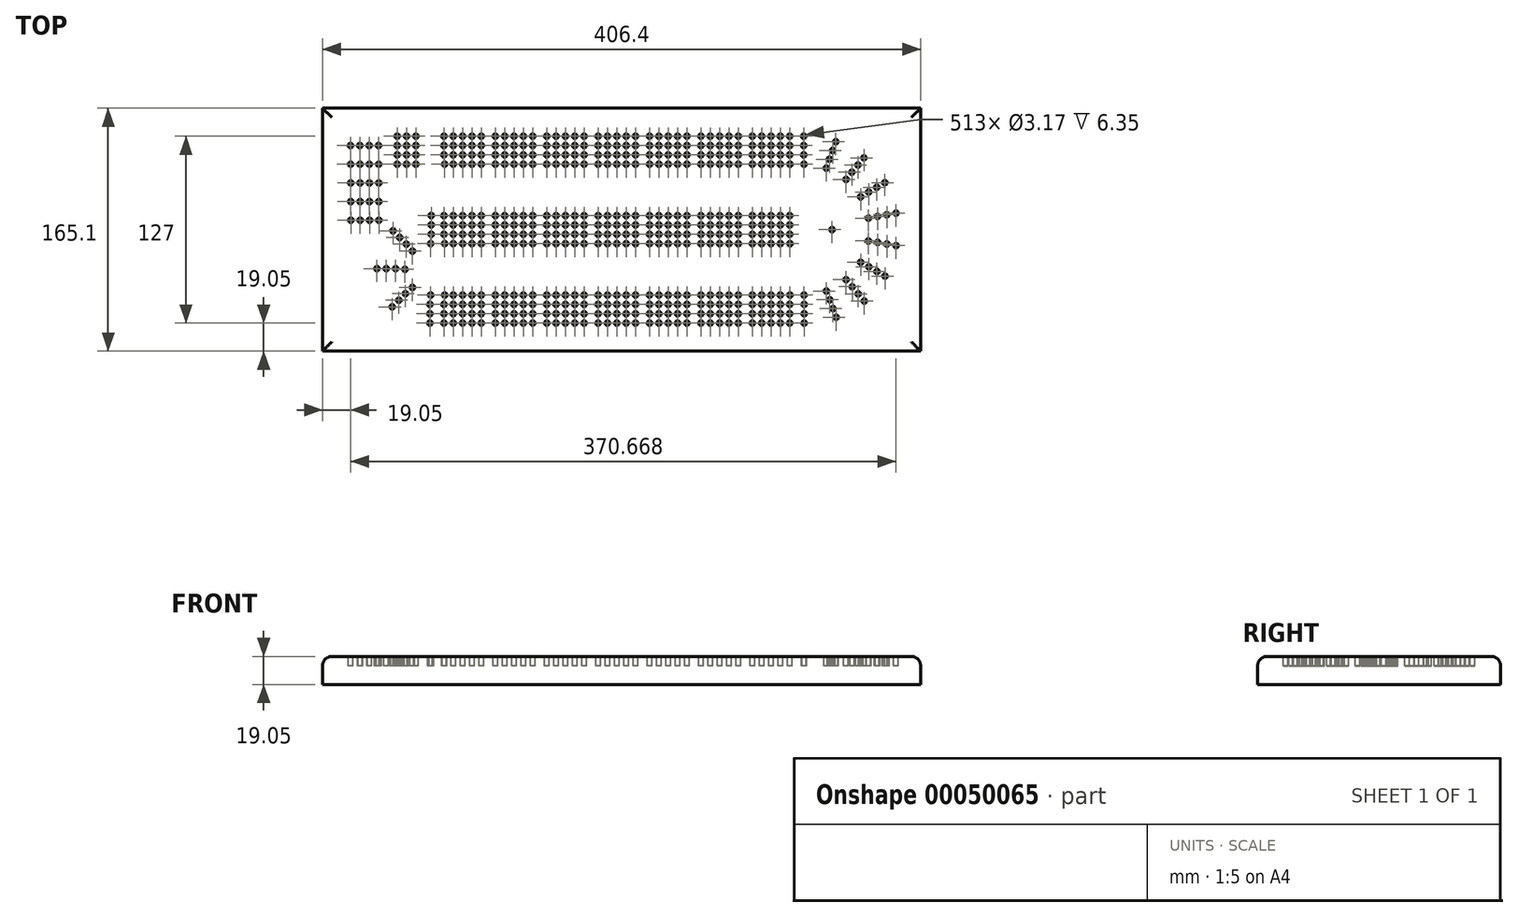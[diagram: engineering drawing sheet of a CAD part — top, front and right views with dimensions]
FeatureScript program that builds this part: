
annotation { "Feature Type Name" : "Feature", "Feature Type Description" : "" }
export const myFeature = defineFeature(function(context is Context, id is Id, definition is map)
    precondition{}
    {
        {
            var Q0;
            Q0=qCreatedBy(makeId("Top.planeOp"),FACE);
            var sketch = newSketch(context, id + "F0", { "sketchPlane" : qUnion([Q0])});
            skLineSegment(sketch, "E0.bottom", {"start": v(0, 0) * mm, "end": v(406.4, 0) * mm});
            skLineSegment(sketch, "E0.top", {"start": v(0, 165.1) * mm, "end": v(406.4, 165.1) * mm});
            skLineSegment(sketch, "E0.left", {"start": v(0, 0) * mm, "end": v(0, 165.1) * mm});
            skLineSegment(sketch, "E0.right", {"start": v(406.4, 0) * mm, "end": v(406.4, 165.1) * mm});
            skSolve(sketch);
        }
        {
            var Q0;
            Q0 = qSketchRegion(id + "F0", true);
            extrude(context, id + "F1", {"entities" : qUnion([Q0]), "depth" : 19.05 * mm});
        }
        {
            var Q0;
            Q0=makeQuery(id+"F1.opExtrude","CAP_EDGE",EDGE,{"disambiguationData":[OSD([sQuery(id+"F0.wireOp",EDGE,"E0.left")])],"isStart":false});
            var Q1;
            Q1=makeQuery(id+"F1.opExtrude","CAP_EDGE",EDGE,{"disambiguationData":[OSD([sQuery(id+"F0.wireOp",EDGE,"E0.top")])],"isStart":false});
            var Q2;
            Q2=makeQuery(id+"F1.opExtrude","CAP_EDGE",EDGE,{"disambiguationData":[OSD([sQuery(id+"F0.wireOp",EDGE,"E0.bottom")])],"isStart":false});
            var Q3;
            Q3=makeQuery(id+"F1.opExtrude","CAP_EDGE",EDGE,{"disambiguationData":[OSD([sQuery(id+"F0.wireOp",EDGE,"E0.right")])],"isStart":false});
            fillet(context, id + "F2", {"entities" : qUnion([Q0, Q1, Q2, Q3]), "radius" : 6.35 * mm, "tangentPropagation" : true, "allowEdgeOverflow" : false});
        }
        {
            var Q0;
            Q0=makeQuery(id+"F1.opExtrude","CAP_FACE",FACE,{"disambiguationData":[OSD([sQuery(id+"F0.wireOp",EDGE,"E0.bottom"),sQuery(id+"F0.wireOp",EDGE,"E0.top"),sQuery(id+"F0.wireOp",EDGE,"E0.left"),sQuery(id+"F0.wireOp",EDGE,"E0.right")])],"isStart":false});
            var sketch = newSketch(context, id + "F3", { "sketchPlane" : qUnion([Q0])});
            skLineSegment(sketch, "E1", {"start": v(6.35, 158.75) * mm, "end": v(6.35, 139.7) * mm});
            skLineSegment(sketch, "E2", {"start": v(6.35, 139.7) * mm, "end": v(19.05, 139.7) * mm});
            skLineSegment(sketch, "E3", {"start": v(19.05, 139.7) * mm, "end": v(25.4, 139.7) * mm});
            skLineSegment(sketch, "E4", {"start": v(25.4, 139.7) * mm, "end": v(31.75, 139.7) * mm});
            skLineSegment(sketch, "E5", {"start": v(31.75, 139.7) * mm, "end": v(38.1, 139.7) * mm});
            skLineSegment(sketch, "E6", {"start": v(6.35, 158.75) * mm, "end": v(50.8, 158.75) * mm});
            skCircle(sketch, "E7", {"center": v(19.05, 139.7) * mm, "radius": 1.59 * mm});
            skCircle(sketch, "E8", {"center": v(25.4, 139.7) * mm, "radius": 1.59 * mm});
            skCircle(sketch, "E9", {"center": v(31.75, 139.7) * mm, "radius": 1.59 * mm});
            skCircle(sketch, "E10", {"center": v(38.1, 139.7) * mm, "radius": 1.59 * mm});
            skCircle(sketch, "E11", {"center": v(50.8, 146.05) * mm, "radius": 1.59 * mm});
            skCircle(sketch, "E12", {"center": v(50.8, 139.7) * mm, "radius": 1.59 * mm});
            skCircle(sketch, "E13", {"center": v(50.8, 133.35) * mm, "radius": 1.59 * mm});
            skCircle(sketch, "E14", {"center": v(50.8, 127) * mm, "radius": 1.59 * mm});
            skCircle(sketch, "E15.1.0.0", {"center": v(31.8, 127) * mm, "radius": 1.59 * mm});
            skCircle(sketch, "E15.1.0.1", {"center": v(25.45, 127) * mm, "radius": 1.59 * mm});
            skCircle(sketch, "E15.1.0.2", {"center": v(19.1, 127) * mm, "radius": 1.59 * mm});
            skCircle(sketch, "E15.1.0.3", {"center": v(38.15, 127) * mm, "radius": 1.59 * mm});
            skCircle(sketch, "E15.2.0.0", {"center": v(31.84, 114.3) * mm, "radius": 1.59 * mm});
            skCircle(sketch, "E15.2.0.1", {"center": v(25.5, 114.3) * mm, "radius": 1.59 * mm});
            skCircle(sketch, "E15.2.0.2", {"center": v(19.14, 114.3) * mm, "radius": 1.59 * mm});
            skCircle(sketch, "E15.2.0.3", {"center": v(38.2, 114.3) * mm, "radius": 1.59 * mm});
            skCircle(sketch, "E15.3.0.0", {"center": v(31.89, 101.6) * mm, "radius": 1.59 * mm});
            skCircle(sketch, "E15.3.0.1", {"center": v(25.54, 101.6) * mm, "radius": 1.59 * mm});
            skCircle(sketch, "E15.3.0.2", {"center": v(19.19, 101.6) * mm, "radius": 1.59 * mm});
            skCircle(sketch, "E15.3.0.3", {"center": v(38.24, 101.6) * mm, "radius": 1.59 * mm});
            skCircle(sketch, "E15.4.0.0", {"center": v(31.93, 88.9) * mm, "radius": 1.59 * mm});
            skCircle(sketch, "E15.4.0.1", {"center": v(25.58, 88.9) * mm, "radius": 1.59 * mm});
            skCircle(sketch, "E15.4.0.2", {"center": v(19.23, 88.9) * mm, "radius": 1.59 * mm});
            skCircle(sketch, "E15.4.0.3", {"center": v(38.28, 88.9) * mm, "radius": 1.59 * mm});
            skLineSegment(sketch, "E15.direction1", {"start": v(31.75, 139.7) * mm, "end": v(31.8, 127) * mm, "construction": true});
            skCircle(sketch, "E16.1.0.0", {"center": v(57.15, 146.05) * mm, "radius": 1.59 * mm});
            skCircle(sketch, "E16.1.0.1", {"center": v(57.15, 139.7) * mm, "radius": 1.59 * mm});
            skCircle(sketch, "E16.1.0.2", {"center": v(57.15, 133.35) * mm, "radius": 1.59 * mm});
            skCircle(sketch, "E16.1.0.3", {"center": v(57.15, 127) * mm, "radius": 1.59 * mm});
            skCircle(sketch, "E16.2.0.0", {"center": v(63.5, 146.05) * mm, "radius": 1.59 * mm});
            skCircle(sketch, "E16.2.0.1", {"center": v(63.5, 139.7) * mm, "radius": 1.59 * mm});
            skCircle(sketch, "E16.2.0.2", {"center": v(63.5, 133.35) * mm, "radius": 1.59 * mm});
            skCircle(sketch, "E16.2.0.3", {"center": v(63.5, 127) * mm, "radius": 1.59 * mm});
            skLineSegment(sketch, "E16.direction1", {"start": v(50.8, 146.05) * mm, "end": v(57.15, 146.05) * mm, "construction": true});
            skCircle(sketch, "E17.1.0.0", {"center": v(95.25, 133.35) * mm, "radius": 1.59 * mm});
            skCircle(sketch, "E17.1.0.1", {"center": v(88.9, 139.7) * mm, "radius": 1.59 * mm});
            skLineSegment(sketch, "E17.1.0.2", {"start": v(82.55, 146.05) * mm, "end": v(88.9, 146.05) * mm, "construction": true});
            skCircle(sketch, "E17.1.0.3", {"center": v(88.9, 146.05) * mm, "radius": 1.59 * mm});
            skCircle(sketch, "E17.1.0.4", {"center": v(82.55, 133.35) * mm, "radius": 1.59 * mm});
            skCircle(sketch, "E17.1.0.5", {"center": v(82.55, 139.7) * mm, "radius": 1.59 * mm});
            skCircle(sketch, "E17.1.0.6", {"center": v(82.55, 146.05) * mm, "radius": 1.59 * mm});
            skCircle(sketch, "E17.1.0.7", {"center": v(95.25, 139.7) * mm, "radius": 1.59 * mm});
            skCircle(sketch, "E17.1.0.8", {"center": v(95.25, 146.05) * mm, "radius": 1.59 * mm});
            skCircle(sketch, "E17.1.0.9", {"center": v(88.9, 133.35) * mm, "radius": 1.59 * mm});
            skCircle(sketch, "E17.1.0.10", {"center": v(82.97, 127) * mm, "radius": 1.59 * mm});
            skCircle(sketch, "E17.1.0.11", {"center": v(95.25, 127) * mm, "radius": 1.59 * mm});
            skCircle(sketch, "E17.1.0.12", {"center": v(88.9, 127) * mm, "radius": 1.59 * mm});
            skCircle(sketch, "E18.1.0.0", {"center": v(101.6, 139.7) * mm, "radius": 1.59 * mm});
            skCircle(sketch, "E18.1.0.2", {"center": v(101.6, 133.35) * mm, "radius": 1.59 * mm});
            skCircle(sketch, "E18.1.0.3", {"center": v(101.6, 127) * mm, "radius": 1.59 * mm});
            skCircle(sketch, "E18.1.0.4", {"center": v(101.6, 146.05) * mm, "radius": 1.59 * mm});
            skCircle(sketch, "E18.2.0.0", {"center": v(107.95, 139.7) * mm, "radius": 1.59 * mm});
            skCircle(sketch, "E18.2.0.2", {"center": v(107.95, 133.35) * mm, "radius": 1.59 * mm});
            skCircle(sketch, "E18.2.0.3", {"center": v(107.95, 127) * mm, "radius": 1.59 * mm});
            skCircle(sketch, "E18.2.0.4", {"center": v(107.95, 146.05) * mm, "radius": 1.59 * mm});
            skCircle(sketch, "E19.1.0.0", {"center": v(142.88, 146.05) * mm, "radius": 1.59 * mm});
            skCircle(sketch, "E19.1.0.1", {"center": v(117.47, 146.05) * mm, "radius": 1.59 * mm});
            skCircle(sketch, "E19.1.0.2", {"center": v(136.52, 139.7) * mm, "radius": 1.59 * mm});
            skCircle(sketch, "E19.1.0.3", {"center": v(123.82, 146.05) * mm, "radius": 1.59 * mm});
            skCircle(sketch, "E19.1.0.4", {"center": v(117.47, 127) * mm, "radius": 1.59 * mm});
            skCircle(sketch, "E19.1.0.6", {"center": v(142.87, 133.35) * mm, "radius": 1.59 * mm});
            skCircle(sketch, "E19.1.0.7", {"center": v(117.47, 133.35) * mm, "radius": 1.59 * mm});
            skCircle(sketch, "E19.1.0.8", {"center": v(130.17, 127) * mm, "radius": 1.59 * mm});
            skCircle(sketch, "E19.1.0.9", {"center": v(123.82, 127) * mm, "radius": 1.59 * mm});
            skCircle(sketch, "E19.1.0.10", {"center": v(142.87, 127) * mm, "radius": 1.59 * mm});
            skCircle(sketch, "E19.1.0.11", {"center": v(117.47, 139.7) * mm, "radius": 1.59 * mm});
            skCircle(sketch, "E19.1.0.13", {"center": v(130.17, 139.7) * mm, "radius": 1.59 * mm});
            skCircle(sketch, "E19.1.0.14", {"center": v(136.52, 133.35) * mm, "radius": 1.59 * mm});
            skCircle(sketch, "E19.1.0.15", {"center": v(136.53, 146.05) * mm, "radius": 1.59 * mm});
            skCircle(sketch, "E19.1.0.16", {"center": v(123.83, 139.7) * mm, "radius": 1.59 * mm});
            skCircle(sketch, "E19.1.0.17", {"center": v(130.18, 146.05) * mm, "radius": 1.59 * mm});
            skLineSegment(sketch, "E19.1.0.18", {"start": v(117.47, 146.05) * mm, "end": v(123.82, 146.05) * mm, "construction": true});
            skCircle(sketch, "E19.1.0.19", {"center": v(123.82, 133.35) * mm, "radius": 1.59 * mm});
            skCircle(sketch, "E19.1.0.20", {"center": v(142.87, 139.7) * mm, "radius": 1.59 * mm});
            skCircle(sketch, "E19.1.0.21", {"center": v(136.52, 127) * mm, "radius": 1.59 * mm});
            skCircle(sketch, "E19.1.0.22", {"center": v(130.17, 133.35) * mm, "radius": 1.59 * mm});
            skCircle(sketch, "E19.2.0.0", {"center": v(177.8, 146.05) * mm, "radius": 1.59 * mm});
            skCircle(sketch, "E19.2.0.1", {"center": v(152.4, 146.05) * mm, "radius": 1.59 * mm});
            skCircle(sketch, "E19.2.0.2", {"center": v(171.45, 139.7) * mm, "radius": 1.59 * mm});
            skCircle(sketch, "E19.2.0.3", {"center": v(158.75, 146.05) * mm, "radius": 1.59 * mm});
            skCircle(sketch, "E19.2.0.4", {"center": v(152.4, 127) * mm, "radius": 1.59 * mm});
            skCircle(sketch, "E19.2.0.6", {"center": v(177.8, 133.35) * mm, "radius": 1.59 * mm});
            skCircle(sketch, "E19.2.0.7", {"center": v(152.4, 133.35) * mm, "radius": 1.59 * mm});
            skCircle(sketch, "E19.2.0.8", {"center": v(165.1, 127) * mm, "radius": 1.59 * mm});
            skCircle(sketch, "E19.2.0.9", {"center": v(158.75, 127) * mm, "radius": 1.59 * mm});
            skCircle(sketch, "E19.2.0.10", {"center": v(177.8, 127) * mm, "radius": 1.59 * mm});
            skCircle(sketch, "E19.2.0.11", {"center": v(152.4, 139.7) * mm, "radius": 1.59 * mm});
            skCircle(sketch, "E19.2.0.13", {"center": v(165.1, 139.7) * mm, "radius": 1.59 * mm});
            skCircle(sketch, "E19.2.0.14", {"center": v(171.45, 133.35) * mm, "radius": 1.59 * mm});
            skCircle(sketch, "E19.2.0.15", {"center": v(171.45, 146.05) * mm, "radius": 1.59 * mm});
            skCircle(sketch, "E19.2.0.16", {"center": v(158.75, 139.7) * mm, "radius": 1.59 * mm});
            skCircle(sketch, "E19.2.0.17", {"center": v(165.1, 146.05) * mm, "radius": 1.59 * mm});
            skCircle(sketch, "E19.2.0.19", {"center": v(158.75, 133.35) * mm, "radius": 1.59 * mm});
            skCircle(sketch, "E19.2.0.20", {"center": v(177.8, 139.7) * mm, "radius": 1.59 * mm});
            skCircle(sketch, "E19.2.0.21", {"center": v(171.45, 127) * mm, "radius": 1.59 * mm});
            skCircle(sketch, "E19.2.0.22", {"center": v(165.1, 133.35) * mm, "radius": 1.59 * mm});
            skCircle(sketch, "E19.3.0.0", {"center": v(212.72, 146.05) * mm, "radius": 1.59 * mm});
            skCircle(sketch, "E19.3.0.1", {"center": v(187.32, 146.05) * mm, "radius": 1.59 * mm});
            skCircle(sketch, "E19.3.0.2", {"center": v(206.37, 139.7) * mm, "radius": 1.59 * mm});
            skCircle(sketch, "E19.3.0.3", {"center": v(193.67, 146.05) * mm, "radius": 1.59 * mm});
            skCircle(sketch, "E19.3.0.4", {"center": v(187.32, 127) * mm, "radius": 1.59 * mm});
            skCircle(sketch, "E19.3.0.6", {"center": v(212.72, 133.35) * mm, "radius": 1.59 * mm});
            skCircle(sketch, "E19.3.0.7", {"center": v(187.32, 133.35) * mm, "radius": 1.59 * mm});
            skCircle(sketch, "E19.3.0.8", {"center": v(200.02, 127) * mm, "radius": 1.59 * mm});
            skCircle(sketch, "E19.3.0.9", {"center": v(193.67, 127) * mm, "radius": 1.59 * mm});
            skCircle(sketch, "E19.3.0.10", {"center": v(212.72, 127) * mm, "radius": 1.59 * mm});
            skCircle(sketch, "E19.3.0.11", {"center": v(187.32, 139.7) * mm, "radius": 1.59 * mm});
            skCircle(sketch, "E19.3.0.13", {"center": v(200.02, 139.7) * mm, "radius": 1.59 * mm});
            skCircle(sketch, "E19.3.0.14", {"center": v(206.37, 133.35) * mm, "radius": 1.59 * mm});
            skCircle(sketch, "E19.3.0.15", {"center": v(206.37, 146.05) * mm, "radius": 1.59 * mm});
            skCircle(sketch, "E19.3.0.16", {"center": v(193.67, 139.7) * mm, "radius": 1.59 * mm});
            skCircle(sketch, "E19.3.0.17", {"center": v(200.02, 146.05) * mm, "radius": 1.59 * mm});
            skCircle(sketch, "E19.3.0.19", {"center": v(193.67, 133.35) * mm, "radius": 1.59 * mm});
            skCircle(sketch, "E19.3.0.20", {"center": v(212.72, 139.7) * mm, "radius": 1.59 * mm});
            skCircle(sketch, "E19.3.0.21", {"center": v(206.37, 127) * mm, "radius": 1.59 * mm});
            skCircle(sketch, "E19.3.0.22", {"center": v(200.02, 133.35) * mm, "radius": 1.59 * mm});
            skCircle(sketch, "E19.4.0.0", {"center": v(247.65, 146.05) * mm, "radius": 1.59 * mm});
            skCircle(sketch, "E19.4.0.1", {"center": v(222.25, 146.05) * mm, "radius": 1.59 * mm});
            skCircle(sketch, "E19.4.0.2", {"center": v(241.3, 139.7) * mm, "radius": 1.59 * mm});
            skCircle(sketch, "E19.4.0.3", {"center": v(228.6, 146.05) * mm, "radius": 1.59 * mm});
            skCircle(sketch, "E19.4.0.4", {"center": v(222.25, 127) * mm, "radius": 1.59 * mm});
            skCircle(sketch, "E19.4.0.6", {"center": v(247.65, 133.35) * mm, "radius": 1.59 * mm});
            skCircle(sketch, "E19.4.0.7", {"center": v(222.25, 133.35) * mm, "radius": 1.59 * mm});
            skCircle(sketch, "E19.4.0.8", {"center": v(234.95, 127) * mm, "radius": 1.59 * mm});
            skCircle(sketch, "E19.4.0.9", {"center": v(228.6, 127) * mm, "radius": 1.59 * mm});
            skCircle(sketch, "E19.4.0.10", {"center": v(247.65, 127) * mm, "radius": 1.59 * mm});
            skCircle(sketch, "E19.4.0.11", {"center": v(222.25, 139.7) * mm, "radius": 1.59 * mm});
            skCircle(sketch, "E19.4.0.13", {"center": v(234.95, 139.7) * mm, "radius": 1.59 * mm});
            skCircle(sketch, "E19.4.0.14", {"center": v(241.3, 133.35) * mm, "radius": 1.59 * mm});
            skCircle(sketch, "E19.4.0.15", {"center": v(241.3, 146.05) * mm, "radius": 1.59 * mm});
            skCircle(sketch, "E19.4.0.16", {"center": v(228.6, 139.7) * mm, "radius": 1.59 * mm});
            skCircle(sketch, "E19.4.0.17", {"center": v(234.95, 146.05) * mm, "radius": 1.59 * mm});
            skCircle(sketch, "E19.4.0.19", {"center": v(228.6, 133.35) * mm, "radius": 1.59 * mm});
            skCircle(sketch, "E19.4.0.20", {"center": v(247.65, 139.7) * mm, "radius": 1.59 * mm});
            skCircle(sketch, "E19.4.0.21", {"center": v(241.3, 127) * mm, "radius": 1.59 * mm});
            skCircle(sketch, "E19.4.0.22", {"center": v(234.95, 133.35) * mm, "radius": 1.59 * mm});
            skCircle(sketch, "E19.5.0.0", {"center": v(282.57, 146.05) * mm, "radius": 1.59 * mm});
            skCircle(sketch, "E19.5.0.1", {"center": v(257.17, 146.05) * mm, "radius": 1.59 * mm});
            skCircle(sketch, "E19.5.0.2", {"center": v(276.22, 139.7) * mm, "radius": 1.59 * mm});
            skCircle(sketch, "E19.5.0.3", {"center": v(263.52, 146.05) * mm, "radius": 1.59 * mm});
            skCircle(sketch, "E19.5.0.4", {"center": v(257.17, 127) * mm, "radius": 1.59 * mm});
            skCircle(sketch, "E19.5.0.6", {"center": v(282.57, 133.35) * mm, "radius": 1.59 * mm});
            skCircle(sketch, "E19.5.0.7", {"center": v(257.17, 133.35) * mm, "radius": 1.59 * mm});
            skCircle(sketch, "E19.5.0.8", {"center": v(269.87, 127) * mm, "radius": 1.59 * mm});
            skCircle(sketch, "E19.5.0.9", {"center": v(263.52, 127) * mm, "radius": 1.59 * mm});
            skCircle(sketch, "E19.5.0.10", {"center": v(282.57, 127) * mm, "radius": 1.59 * mm});
            skCircle(sketch, "E19.5.0.11", {"center": v(257.17, 139.7) * mm, "radius": 1.59 * mm});
            skCircle(sketch, "E19.5.0.13", {"center": v(269.87, 139.7) * mm, "radius": 1.59 * mm});
            skCircle(sketch, "E19.5.0.14", {"center": v(276.22, 133.35) * mm, "radius": 1.59 * mm});
            skCircle(sketch, "E19.5.0.15", {"center": v(276.22, 146.05) * mm, "radius": 1.59 * mm});
            skCircle(sketch, "E19.5.0.16", {"center": v(263.52, 139.7) * mm, "radius": 1.59 * mm});
            skCircle(sketch, "E19.5.0.17", {"center": v(269.88, 146.05) * mm, "radius": 1.59 * mm});
            skCircle(sketch, "E19.5.0.19", {"center": v(263.52, 133.35) * mm, "radius": 1.59 * mm});
            skCircle(sketch, "E19.5.0.20", {"center": v(282.57, 139.7) * mm, "radius": 1.59 * mm});
            skCircle(sketch, "E19.5.0.21", {"center": v(276.22, 127) * mm, "radius": 1.59 * mm});
            skCircle(sketch, "E19.5.0.22", {"center": v(269.87, 133.35) * mm, "radius": 1.59 * mm});
            skCircle(sketch, "E20.0.6.0", {"center": v(317.5, 146.05) * mm, "radius": 1.59 * mm});
            skCircle(sketch, "E20.2.6.0", {"center": v(292.1, 146.05) * mm, "radius": 1.59 * mm});
            skCircle(sketch, "E20.4.6.0", {"center": v(311.15, 139.7) * mm, "radius": 1.59 * mm});
            skCircle(sketch, "E20.6.6.0", {"center": v(298.45, 146.05) * mm, "radius": 1.59 * mm});
            skCircle(sketch, "E20.8.6.0", {"center": v(292.1, 127) * mm, "radius": 1.59 * mm});
            skCircle(sketch, "E20.13.6.0", {"center": v(317.5, 133.35) * mm, "radius": 1.59 * mm});
            skCircle(sketch, "E20.15.6.0", {"center": v(292.1, 133.35) * mm, "radius": 1.59 * mm});
            skCircle(sketch, "E20.17.6.0", {"center": v(304.8, 127) * mm, "radius": 1.59 * mm});
            skCircle(sketch, "E20.19.6.0", {"center": v(298.45, 127) * mm, "radius": 1.59 * mm});
            skCircle(sketch, "E20.21.6.0", {"center": v(317.63, 127) * mm, "radius": 1.59 * mm});
            skCircle(sketch, "E20.23.6.0", {"center": v(292.1, 139.7) * mm, "radius": 1.59 * mm});
            skCircle(sketch, "E20.28.6.0", {"center": v(304.8, 139.7) * mm, "radius": 1.59 * mm});
            skCircle(sketch, "E20.30.6.0", {"center": v(311.15, 133.35) * mm, "radius": 1.59 * mm});
            skCircle(sketch, "E20.32.6.0", {"center": v(311.15, 146.05) * mm, "radius": 1.59 * mm});
            skCircle(sketch, "E20.34.6.0", {"center": v(298.45, 139.7) * mm, "radius": 1.59 * mm});
            skCircle(sketch, "E20.36.6.0", {"center": v(304.8, 146.05) * mm, "radius": 1.59 * mm});
            skCircle(sketch, "E20.41.6.0", {"center": v(298.45, 133.35) * mm, "radius": 1.59 * mm});
            skCircle(sketch, "E20.43.6.0", {"center": v(317.5, 139.7) * mm, "radius": 1.59 * mm});
            skCircle(sketch, "E20.45.6.0", {"center": v(311.15, 127) * mm, "radius": 1.59 * mm});
            skCircle(sketch, "E20.47.6.0", {"center": v(304.8, 133.35) * mm, "radius": 1.59 * mm});
            skLineSegment(sketch, "E21", {"start": v(327.16, 82.55) * mm, "end": v(327.16, 6.35) * mm});
            skLineSegment(sketch, "E22", {"start": v(327.16, 82.55) * mm, "end": v(400.05, 82.55) * mm});
            skCircle(sketch, "E23.1.0.0", {"center": v(327.16, 127) * mm, "radius": 1.59 * mm});
            skCircle(sketch, "E23.1.0.1", {"center": v(327.02, 133.35) * mm, "radius": 1.59 * mm});
            skCircle(sketch, "E23.1.0.2", {"center": v(327.02, 139.7) * mm, "radius": 1.59 * mm});
            skCircle(sketch, "E23.1.0.3", {"center": v(327.02, 146.05) * mm, "radius": 1.59 * mm});
            skLineSegment(sketch, "E23.direction1", {"start": v(317.63, 127) * mm, "end": v(327.16, 127) * mm, "construction": true});
            skLineSegment(sketch, "E24.1.0", {"start": v(333.41, 127.58) * mm, "end": v(342.36, 124.32) * mm, "construction": true});
            skCircle(sketch, "E24.1.1", {"center": v(348.75, 142.27) * mm, "radius": 1.59 * mm});
            skCircle(sketch, "E24.1.2", {"center": v(346.58, 136.3) * mm, "radius": 1.59 * mm});
            skCircle(sketch, "E24.1.3", {"center": v(342.36, 124.32) * mm, "radius": 1.59 * mm});
            skCircle(sketch, "E24.1.4", {"center": v(344.4, 130.33) * mm, "radius": 1.59 * mm});
            skLineSegment(sketch, "E24.2.0", {"start": v(348.44, 122.72) * mm, "end": v(355.73, 116.6) * mm, "construction": true});
            skCircle(sketch, "E24.2.1", {"center": v(367.87, 131.28) * mm, "radius": 1.59 * mm});
            skCircle(sketch, "E24.2.2", {"center": v(363.8, 126.42) * mm, "radius": 1.59 * mm});
            skCircle(sketch, "E24.2.3", {"center": v(355.73, 116.6) * mm, "radius": 1.59 * mm});
            skCircle(sketch, "E24.2.4", {"center": v(359.71, 121.55) * mm, "radius": 1.59 * mm});
            skLineSegment(sketch, "E24.3.0", {"start": v(360.9, 113.02) * mm, "end": v(365.65, 104.78) * mm, "construction": true});
            skCircle(sketch, "E24.3.1", {"center": v(382.09, 114.42) * mm, "radius": 1.59 * mm});
            skCircle(sketch, "E24.3.2", {"center": v(376.59, 111.24) * mm, "radius": 1.59 * mm});
            skCircle(sketch, "E24.3.3", {"center": v(365.65, 104.78) * mm, "radius": 1.59 * mm});
            skCircle(sketch, "E24.3.4", {"center": v(371.09, 108.07) * mm, "radius": 1.59 * mm});
            skLineSegment(sketch, "E24.4.0", {"start": v(369.28, 99.65) * mm, "end": v(370.93, 90.27) * mm, "construction": true});
            skCircle(sketch, "E24.4.1", {"center": v(389.67, 93.7) * mm, "radius": 1.59 * mm});
            skCircle(sketch, "E24.4.2", {"center": v(383.42, 92.6) * mm, "radius": 1.59 * mm});
            skCircle(sketch, "E24.4.3", {"center": v(370.93, 90.27) * mm, "radius": 1.59 * mm});
            skCircle(sketch, "E24.4.4", {"center": v(377.16, 91.5) * mm, "radius": 1.59 * mm});
            skLineSegment(sketch, "E24.5.0", {"start": v(372.59, 84.21) * mm, "end": v(370.93, 74.83) * mm, "construction": true});
            skCircle(sketch, "E24.5.1", {"center": v(389.72, 71.66) * mm, "radius": 1.59 * mm});
            skCircle(sketch, "E24.5.2", {"center": v(383.46, 72.76) * mm, "radius": 1.59 * mm});
            skCircle(sketch, "E24.5.3", {"center": v(370.93, 74.83) * mm, "radius": 1.59 * mm});
            skCircle(sketch, "E24.5.4", {"center": v(377.21, 73.86) * mm, "radius": 1.59 * mm});
            skLineSegment(sketch, "E24.6.0", {"start": v(370.42, 68.57) * mm, "end": v(365.65, 60.32) * mm, "construction": true});
            skCircle(sketch, "E24.6.1", {"center": v(382.22, 50.92) * mm, "radius": 1.59 * mm});
            skCircle(sketch, "E24.6.2", {"center": v(376.72, 54.1) * mm, "radius": 1.59 * mm});
            skCircle(sketch, "E24.6.3", {"center": v(365.65, 60.32) * mm, "radius": 1.59 * mm});
            skCircle(sketch, "E24.6.4", {"center": v(371.22, 57.27) * mm, "radius": 1.59 * mm});
            skLineSegment(sketch, "E24.7.0", {"start": v(363.03, 54.62) * mm, "end": v(355.73, 48.5) * mm, "construction": true});
            skCircle(sketch, "E24.7.1", {"center": v(368.08, 34) * mm, "radius": 1.59 * mm});
            skCircle(sketch, "E24.7.2", {"center": v(364, 38.86) * mm, "radius": 1.59 * mm});
            skCircle(sketch, "E24.7.3", {"center": v(355.73, 48.5) * mm, "radius": 1.59 * mm});
            skCircle(sketch, "E24.7.4", {"center": v(359.92, 43.72) * mm, "radius": 1.59 * mm});
            skLineSegment(sketch, "E24.8.0", {"start": v(351.31, 44.04) * mm, "end": v(342.36, 40.78) * mm, "construction": true});
            skCircle(sketch, "E24.8.1", {"center": v(349, 22.93) * mm, "radius": 1.59 * mm});
            skCircle(sketch, "E24.8.2", {"center": v(346.83, 28.9) * mm, "radius": 1.59 * mm});
            skCircle(sketch, "E24.8.3", {"center": v(342.36, 40.78) * mm, "radius": 1.59 * mm});
            skCircle(sketch, "E24.8.4", {"center": v(344.66, 34.86) * mm, "radius": 1.59 * mm});
            skLineSegment(sketch, "E24.9.0", {"start": v(336.68, 38.1) * mm, "end": v(327.16, 38.1) * mm, "construction": true});
            skCircle(sketch, "E24.9.1", {"center": v(327.3, 19.05) * mm, "radius": 1.59 * mm});
            skCircle(sketch, "E24.9.2", {"center": v(327.3, 25.4) * mm, "radius": 1.59 * mm});
            skCircle(sketch, "E24.9.3", {"center": v(327.16, 38.1) * mm, "radius": 1.59 * mm});
            skCircle(sketch, "E24.9.4", {"center": v(327.3, 31.75) * mm, "radius": 1.59 * mm});
            skPoint(sketch, "E24.center", {"position": v(327.16, 82.55) * mm});
            skLineSegment(sketch, "E24.anchor1", {"start": v(327.16, 82.55) * mm, "end": v(327.16, 127) * mm, "construction": true});
            skLineSegment(sketch, "E24.anchor2", {"start": v(327.16, 82.55) * mm, "end": v(327.16, 38.1) * mm, "construction": true});
            skCircle(sketch, "E25.MirrorC", {"center": v(317.5, 19.05) * mm, "radius": 1.59 * mm});
            skLineSegment(sketch, "E26.MirrorCS", {"start": v(317.63, 38.1) * mm, "end": v(327.16, 38.1) * mm, "construction": true});
            skCircle(sketch, "E27.MirrorC", {"center": v(311.15, 25.4) * mm, "radius": 1.59 * mm});
            skCircle(sketch, "E28.MirrorC", {"center": v(317.5, 25.4) * mm, "radius": 1.59 * mm});
            skCircle(sketch, "E29.MirrorC", {"center": v(276.22, 25.4) * mm, "radius": 1.59 * mm});
            skCircle(sketch, "E30.MirrorC", {"center": v(95.25, 19.05) * mm, "radius": 1.59 * mm});
            skCircle(sketch, "E31.MirrorC", {"center": v(123.83, 19.05) * mm, "radius": 1.59 * mm});
            skCircle(sketch, "E32.MirrorC", {"center": v(257.18, 19.05) * mm, "radius": 1.59 * mm});
            skCircle(sketch, "E33.MirrorC", {"center": v(282.57, 25.4) * mm, "radius": 1.59 * mm});
            skCircle(sketch, "E34.MirrorC", {"center": v(311.15, 19.05) * mm, "radius": 1.59 * mm});
            skCircle(sketch, "E35.MirrorC", {"center": v(142.87, 25.4) * mm, "radius": 1.59 * mm});
            skCircle(sketch, "E36.MirrorC", {"center": v(171.45, 19.05) * mm, "radius": 1.59 * mm});
            skCircle(sketch, "E37.MirrorC", {"center": v(95.25, 25.4) * mm, "radius": 1.59 * mm});
            skCircle(sketch, "E38.MirrorC", {"center": v(136.52, 25.4) * mm, "radius": 1.59 * mm});
            skCircle(sketch, "E39.MirrorC", {"center": v(171.45, 31.75) * mm, "radius": 1.59 * mm});
            skCircle(sketch, "E40.MirrorC", {"center": v(117.48, 19.05) * mm, "radius": 1.59 * mm});
            skCircle(sketch, "E41.MirrorC", {"center": v(95.25, 31.75) * mm, "radius": 1.59 * mm});
            skCircle(sketch, "E42.MirrorC", {"center": v(263.52, 31.75) * mm, "radius": 1.59 * mm});
            skCircle(sketch, "E43.MirrorC", {"center": v(311.15, 31.75) * mm, "radius": 1.59 * mm});
            skCircle(sketch, "E44.MirrorC", {"center": v(269.88, 19.05) * mm, "radius": 1.59 * mm});
            skCircle(sketch, "E45.MirrorC", {"center": v(304.8, 25.4) * mm, "radius": 1.59 * mm});
            skLineSegment(sketch, "E46.MirrorCS", {"start": v(117.48, 19.05) * mm, "end": v(123.83, 19.05) * mm, "construction": true});
            skCircle(sketch, "E47.MirrorC", {"center": v(165.1, 25.4) * mm, "radius": 1.59 * mm});
            skCircle(sketch, "E48.MirrorC", {"center": v(228.6, 19.05) * mm, "radius": 1.59 * mm});
            skCircle(sketch, "E49.MirrorC", {"center": v(228.6, 25.4) * mm, "radius": 1.59 * mm});
            skCircle(sketch, "E50.MirrorC", {"center": v(257.18, 25.4) * mm, "radius": 1.59 * mm});
            skCircle(sketch, "E51.MirrorC", {"center": v(241.3, 19.05) * mm, "radius": 1.59 * mm});
            skCircle(sketch, "E52.MirrorC", {"center": v(317.5, 31.75) * mm, "radius": 1.59 * mm});
            skCircle(sketch, "E53.MirrorC", {"center": v(117.48, 25.4) * mm, "radius": 1.59 * mm});
            skCircle(sketch, "E54.MirrorC", {"center": v(101.6, 38.1) * mm, "radius": 1.59 * mm});
            skCircle(sketch, "E55.MirrorC", {"center": v(177.8, 31.75) * mm, "radius": 1.59 * mm});
            skCircle(sketch, "E56.MirrorC", {"center": v(298.45, 31.75) * mm, "radius": 1.59 * mm});
            skCircle(sketch, "E57.MirrorC", {"center": v(101.6, 19.05) * mm, "radius": 1.59 * mm});
            skCircle(sketch, "E58.MirrorC", {"center": v(263.53, 25.4) * mm, "radius": 1.59 * mm});
            skCircle(sketch, "E59.MirrorC", {"center": v(292.1, 25.4) * mm, "radius": 1.59 * mm});
            skCircle(sketch, "E60.MirrorC", {"center": v(130.17, 25.4) * mm, "radius": 1.59 * mm});
            skCircle(sketch, "E61.MirrorC", {"center": v(177.8, 19.05) * mm, "radius": 1.59 * mm});
            skCircle(sketch, "E62.MirrorC", {"center": v(130.18, 19.05) * mm, "radius": 1.59 * mm});
            skCircle(sketch, "E63.MirrorC", {"center": v(241.3, 25.4) * mm, "radius": 1.59 * mm});
            skCircle(sketch, "E64.MirrorC", {"center": v(158.75, 31.75) * mm, "radius": 1.59 * mm});
            skCircle(sketch, "E65.MirrorC", {"center": v(107.95, 19.05) * mm, "radius": 1.59 * mm});
            skCircle(sketch, "E66.MirrorC", {"center": v(317.63, 38.1) * mm, "radius": 1.59 * mm});
            skCircle(sketch, "E67.MirrorC", {"center": v(123.83, 25.4) * mm, "radius": 1.59 * mm});
            skCircle(sketch, "E68.MirrorC", {"center": v(222.25, 19.05) * mm, "radius": 1.59 * mm});
            skCircle(sketch, "E69.MirrorC", {"center": v(142.87, 31.75) * mm, "radius": 1.59 * mm});
            skCircle(sketch, "E70.MirrorC", {"center": v(101.6, 31.75) * mm, "radius": 1.59 * mm});
            skCircle(sketch, "E71.MirrorC", {"center": v(304.8, 31.75) * mm, "radius": 1.59 * mm});
            skCircle(sketch, "E72.MirrorC", {"center": v(88.9, 19.05) * mm, "radius": 1.59 * mm});
            skCircle(sketch, "E73.MirrorC", {"center": v(234.95, 25.4) * mm, "radius": 1.59 * mm});
            skCircle(sketch, "E74.MirrorC", {"center": v(101.6, 25.4) * mm, "radius": 1.59 * mm});
            skCircle(sketch, "E75.MirrorC", {"center": v(165.1, 31.75) * mm, "radius": 1.59 * mm});
            skCircle(sketch, "E76.MirrorC", {"center": v(276.22, 31.75) * mm, "radius": 1.59 * mm});
            skCircle(sketch, "E77.MirrorC", {"center": v(311.15, 38.1) * mm, "radius": 1.59 * mm});
            skCircle(sketch, "E78.MirrorC", {"center": v(222.25, 25.4) * mm, "radius": 1.59 * mm});
            skCircle(sketch, "E79.MirrorC", {"center": v(158.75, 38.1) * mm, "radius": 1.59 * mm});
            skCircle(sketch, "E80.MirrorC", {"center": v(107.95, 31.75) * mm, "radius": 1.59 * mm});
            skLineSegment(sketch, "E81.MirrorCS", {"start": v(82.55, 19.05) * mm, "end": v(88.9, 19.05) * mm, "construction": true});
            skCircle(sketch, "E82.MirrorC", {"center": v(263.53, 19.05) * mm, "radius": 1.59 * mm});
            skCircle(sketch, "E83.MirrorC", {"center": v(269.87, 31.75) * mm, "radius": 1.59 * mm});
            skCircle(sketch, "E84.MirrorC", {"center": v(234.95, 19.05) * mm, "radius": 1.59 * mm});
            skCircle(sketch, "E85.MirrorC", {"center": v(304.8, 38.1) * mm, "radius": 1.59 * mm});
            skCircle(sketch, "E86.MirrorC", {"center": v(269.87, 25.4) * mm, "radius": 1.59 * mm});
            skCircle(sketch, "E87.MirrorC", {"center": v(165.1, 19.05) * mm, "radius": 1.59 * mm});
            skCircle(sketch, "E88.MirrorC", {"center": v(136.52, 31.75) * mm, "radius": 1.59 * mm});
            skCircle(sketch, "E89.MirrorC", {"center": v(107.95, 25.4) * mm, "radius": 1.59 * mm});
            skCircle(sketch, "E90.MirrorC", {"center": v(88.9, 38.1) * mm, "radius": 1.59 * mm});
            skCircle(sketch, "E91.MirrorC", {"center": v(171.45, 25.4) * mm, "radius": 1.59 * mm});
            skCircle(sketch, "E92.MirrorC", {"center": v(88.9, 31.75) * mm, "radius": 1.59 * mm});
            skCircle(sketch, "E93.MirrorC", {"center": v(282.57, 31.75) * mm, "radius": 1.59 * mm});
            skCircle(sketch, "E94.MirrorC", {"center": v(95.25, 38.1) * mm, "radius": 1.59 * mm});
            skCircle(sketch, "E95.MirrorC", {"center": v(177.8, 25.4) * mm, "radius": 1.59 * mm});
            skCircle(sketch, "E96.MirrorC", {"center": v(117.47, 31.75) * mm, "radius": 1.59 * mm});
            skCircle(sketch, "E97.MirrorC", {"center": v(276.22, 38.1) * mm, "radius": 1.59 * mm});
            skCircle(sketch, "E98.MirrorC", {"center": v(298.45, 25.4) * mm, "radius": 1.59 * mm});
            skCircle(sketch, "E99.MirrorC", {"center": v(158.75, 25.4) * mm, "radius": 1.59 * mm});
            skCircle(sketch, "E100.MirrorC", {"center": v(187.33, 25.4) * mm, "radius": 1.59 * mm});
            skCircle(sketch, "E101.MirrorC", {"center": v(222.25, 31.75) * mm, "radius": 1.59 * mm});
            skCircle(sketch, "E102.MirrorC", {"center": v(212.72, 38.1) * mm, "radius": 1.59 * mm});
            skCircle(sketch, "E103.MirrorC", {"center": v(247.65, 31.75) * mm, "radius": 1.59 * mm});
            skCircle(sketch, "E104.MirrorC", {"center": v(123.82, 31.75) * mm, "radius": 1.59 * mm});
            skCircle(sketch, "E105.MirrorC", {"center": v(193.68, 38.1) * mm, "radius": 1.59 * mm});
            skCircle(sketch, "E106.MirrorC", {"center": v(222.25, 38.1) * mm, "radius": 1.59 * mm});
            skCircle(sketch, "E107.MirrorC", {"center": v(82.55, 19.05) * mm, "radius": 1.59 * mm});
            skCircle(sketch, "E108.MirrorC", {"center": v(206.37, 25.4) * mm, "radius": 1.59 * mm});
            skCircle(sketch, "E109.MirrorC", {"center": v(152.4, 31.75) * mm, "radius": 1.59 * mm});
            skCircle(sketch, "E110.MirrorC", {"center": v(282.58, 19.05) * mm, "radius": 1.59 * mm});
            skCircle(sketch, "E111.MirrorC", {"center": v(82.55, 25.4) * mm, "radius": 1.59 * mm});
            skCircle(sketch, "E112.MirrorC", {"center": v(142.88, 19.05) * mm, "radius": 1.59 * mm});
            skCircle(sketch, "E113.MirrorC", {"center": v(234.95, 31.75) * mm, "radius": 1.59 * mm});
            skCircle(sketch, "E114.MirrorC", {"center": v(200.03, 38.1) * mm, "radius": 1.59 * mm});
            skCircle(sketch, "E115.MirrorC", {"center": v(206.38, 38.1) * mm, "radius": 1.59 * mm});
            skCircle(sketch, "E116.MirrorC", {"center": v(212.72, 25.4) * mm, "radius": 1.59 * mm});
            skCircle(sketch, "E117.MirrorC", {"center": v(257.18, 38.1) * mm, "radius": 1.59 * mm});
            skCircle(sketch, "E118.MirrorC", {"center": v(292.1, 31.75) * mm, "radius": 1.59 * mm});
            skCircle(sketch, "E119.MirrorC", {"center": v(187.33, 19.05) * mm, "radius": 1.59 * mm});
            skCircle(sketch, "E120.MirrorC", {"center": v(241.3, 38.1) * mm, "radius": 1.59 * mm});
            skCircle(sketch, "E121.MirrorC", {"center": v(152.4, 25.4) * mm, "radius": 1.59 * mm});
            skCircle(sketch, "E122.MirrorC", {"center": v(187.32, 31.75) * mm, "radius": 1.59 * mm});
            skCircle(sketch, "E123.MirrorC", {"center": v(206.37, 31.75) * mm, "radius": 1.59 * mm});
            skCircle(sketch, "E124.MirrorC", {"center": v(247.65, 25.4) * mm, "radius": 1.59 * mm});
            skCircle(sketch, "E125.MirrorC", {"center": v(228.6, 38.1) * mm, "radius": 1.59 * mm});
            skCircle(sketch, "E126.MirrorC", {"center": v(276.23, 19.05) * mm, "radius": 1.59 * mm});
            skCircle(sketch, "E127.MirrorC", {"center": v(177.8, 38.1) * mm, "radius": 1.59 * mm});
            skCircle(sketch, "E128.MirrorC", {"center": v(212.72, 31.75) * mm, "radius": 1.59 * mm});
            skCircle(sketch, "E129.MirrorC", {"center": v(82.97, 38.1) * mm, "radius": 1.59 * mm});
            skCircle(sketch, "E130.MirrorC", {"center": v(241.3, 31.75) * mm, "radius": 1.59 * mm});
            skCircle(sketch, "E131.MirrorC", {"center": v(193.67, 31.75) * mm, "radius": 1.59 * mm});
            skCircle(sketch, "E132.MirrorC", {"center": v(263.52, 38.1) * mm, "radius": 1.59 * mm});
            skCircle(sketch, "E133.MirrorC", {"center": v(292.1, 38.1) * mm, "radius": 1.59 * mm});
            skCircle(sketch, "E134.MirrorC", {"center": v(212.73, 19.05) * mm, "radius": 1.59 * mm});
            skCircle(sketch, "E135.MirrorC", {"center": v(152.4, 38.1) * mm, "radius": 1.59 * mm});
            skCircle(sketch, "E136.MirrorC", {"center": v(107.95, 38.1) * mm, "radius": 1.59 * mm});
            skCircle(sketch, "E137.MirrorC", {"center": v(200.03, 19.05) * mm, "radius": 1.59 * mm});
            skCircle(sketch, "E138.MirrorC", {"center": v(298.45, 19.05) * mm, "radius": 1.59 * mm});
            skCircle(sketch, "E139.MirrorC", {"center": v(269.87, 38.1) * mm, "radius": 1.59 * mm});
            skCircle(sketch, "E140.MirrorC", {"center": v(123.83, 38.1) * mm, "radius": 1.59 * mm});
            skCircle(sketch, "E141.MirrorC", {"center": v(158.75, 19.05) * mm, "radius": 1.59 * mm});
            skCircle(sketch, "E142.MirrorC", {"center": v(228.6, 31.75) * mm, "radius": 1.59 * mm});
            skCircle(sketch, "E143.MirrorC", {"center": v(298.45, 38.1) * mm, "radius": 1.59 * mm});
            skCircle(sketch, "E144.MirrorC", {"center": v(193.68, 25.4) * mm, "radius": 1.59 * mm});
            skCircle(sketch, "E145.MirrorC", {"center": v(136.53, 19.05) * mm, "radius": 1.59 * mm});
            skCircle(sketch, "E146.MirrorC", {"center": v(257.17, 31.75) * mm, "radius": 1.59 * mm});
            skCircle(sketch, "E147.MirrorC", {"center": v(187.33, 38.1) * mm, "radius": 1.59 * mm});
            skCircle(sketch, "E148.MirrorC", {"center": v(247.65, 19.05) * mm, "radius": 1.59 * mm});
            skCircle(sketch, "E149.MirrorC", {"center": v(304.8, 19.05) * mm, "radius": 1.59 * mm});
            skCircle(sketch, "E150.MirrorC", {"center": v(130.17, 31.75) * mm, "radius": 1.59 * mm});
            skCircle(sketch, "E151.MirrorC", {"center": v(165.1, 38.1) * mm, "radius": 1.59 * mm});
            skCircle(sketch, "E152.MirrorC", {"center": v(193.68, 19.05) * mm, "radius": 1.59 * mm});
            skCircle(sketch, "E153.MirrorC", {"center": v(200.02, 31.75) * mm, "radius": 1.59 * mm});
            skCircle(sketch, "E154.MirrorC", {"center": v(200.02, 25.4) * mm, "radius": 1.59 * mm});
            skCircle(sketch, "E155.MirrorC", {"center": v(88.9, 25.4) * mm, "radius": 1.59 * mm});
            skCircle(sketch, "E156.MirrorC", {"center": v(130.18, 38.1) * mm, "radius": 1.59 * mm});
            skCircle(sketch, "E157.MirrorC", {"center": v(171.45, 38.1) * mm, "radius": 1.59 * mm});
            skCircle(sketch, "E158.MirrorC", {"center": v(117.48, 38.1) * mm, "radius": 1.59 * mm});
            skCircle(sketch, "E159.MirrorC", {"center": v(206.38, 19.05) * mm, "radius": 1.59 * mm});
            skCircle(sketch, "E160.MirrorC", {"center": v(247.65, 38.1) * mm, "radius": 1.59 * mm});
            skCircle(sketch, "E161.MirrorC", {"center": v(292.1, 19.05) * mm, "radius": 1.59 * mm});
            skCircle(sketch, "E162.MirrorC", {"center": v(152.4, 19.05) * mm, "radius": 1.59 * mm});
            skCircle(sketch, "E163.MirrorC", {"center": v(136.53, 38.1) * mm, "radius": 1.59 * mm});
            skCircle(sketch, "E164.MirrorC", {"center": v(282.57, 38.1) * mm, "radius": 1.59 * mm});
            skCircle(sketch, "E165.MirrorC", {"center": v(82.55, 31.75) * mm, "radius": 1.59 * mm});
            skCircle(sketch, "E166.MirrorC", {"center": v(142.88, 38.1) * mm, "radius": 1.59 * mm});
            skCircle(sketch, "E167.MirrorC", {"center": v(234.95, 38.1) * mm, "radius": 1.59 * mm});
            skLineSegment(sketch, "E168", {"start": v(317.63, 38.1) * mm, "end": v(317.63, 55.56) * mm});
            skLineSegment(sketch, "E169", {"start": v(317.63, 55.56) * mm, "end": v(289.22, 55.56) * mm});
            skCircle(sketch, "E170.MirrorC", {"center": v(317.63, 73.02) * mm, "radius": 1.59 * mm});
            skLineSegment(sketch, "E171.MirrorCS", {"start": v(317.63, 73.02) * mm, "end": v(317.63, 55.56) * mm});
            skLineSegment(sketch, "E172.MirrorCS", {"start": v(317.63, 73.02) * mm, "end": v(327.16, 73.02) * mm, "construction": true});
            skLineSegment(sketch, "E173.MirrorCS", {"start": v(117.48, 92.08) * mm, "end": v(123.83, 92.08) * mm, "construction": true});
            skCircle(sketch, "E174.MirrorC", {"center": v(123.83, 92.08) * mm, "radius": 1.59 * mm});
            skCircle(sketch, "E175.MirrorC", {"center": v(117.48, 92.08) * mm, "radius": 1.59 * mm});
            skCircle(sketch, "E176.MirrorC", {"center": v(88.9, 92.08) * mm, "radius": 1.59 * mm});
            skCircle(sketch, "E177.MirrorC", {"center": v(82.55, 92.08) * mm, "radius": 1.59 * mm});
            skLineSegment(sketch, "E178.MirrorCS", {"start": v(82.55, 92.08) * mm, "end": v(88.9, 92.08) * mm, "construction": true});
            skCircle(sketch, "E179.MirrorC", {"center": v(82.55, 79.37) * mm, "radius": 1.59 * mm});
            skCircle(sketch, "E180.MirrorC", {"center": v(222.25, 79.37) * mm, "radius": 1.59 * mm});
            skCircle(sketch, "E181.MirrorC", {"center": v(257.18, 73.02) * mm, "radius": 1.59 * mm});
            skCircle(sketch, "E182.MirrorC", {"center": v(292.1, 73.02) * mm, "radius": 1.59 * mm});
            skCircle(sketch, "E183.MirrorC", {"center": v(304.8, 92.07) * mm, "radius": 1.59 * mm});
            skCircle(sketch, "E184.MirrorC", {"center": v(95.25, 85.72) * mm, "radius": 1.59 * mm});
            skCircle(sketch, "E185.MirrorC", {"center": v(117.48, 85.72) * mm, "radius": 1.59 * mm});
            skCircle(sketch, "E186.MirrorC", {"center": v(142.87, 79.37) * mm, "radius": 1.59 * mm});
            skCircle(sketch, "E187.MirrorC", {"center": v(304.8, 73.02) * mm, "radius": 1.59 * mm});
            skCircle(sketch, "E188.MirrorC", {"center": v(282.57, 73.02) * mm, "radius": 1.59 * mm});
            skCircle(sketch, "E189.MirrorC", {"center": v(187.33, 85.72) * mm, "radius": 1.59 * mm});
            skCircle(sketch, "E190.MirrorC", {"center": v(212.72, 85.72) * mm, "radius": 1.59 * mm});
            skCircle(sketch, "E191.MirrorC", {"center": v(263.52, 73.02) * mm, "radius": 1.59 * mm});
            skCircle(sketch, "E192.MirrorC", {"center": v(247.65, 92.07) * mm, "radius": 1.59 * mm});
            skCircle(sketch, "E193.MirrorC", {"center": v(171.45, 92.08) * mm, "radius": 1.59 * mm});
            skCircle(sketch, "E194.MirrorC", {"center": v(317.5, 79.37) * mm, "radius": 1.59 * mm});
            skCircle(sketch, "E195.MirrorC", {"center": v(222.25, 92.07) * mm, "radius": 1.59 * mm});
            skCircle(sketch, "E196.MirrorC", {"center": v(234.95, 92.07) * mm, "radius": 1.59 * mm});
            skCircle(sketch, "E197.MirrorC", {"center": v(136.53, 73.03) * mm, "radius": 1.59 * mm});
            skCircle(sketch, "E198.MirrorC", {"center": v(158.75, 85.72) * mm, "radius": 1.59 * mm});
            skCircle(sketch, "E199.MirrorC", {"center": v(206.38, 73.02) * mm, "radius": 1.59 * mm});
            skCircle(sketch, "E200.MirrorC", {"center": v(193.67, 79.37) * mm, "radius": 1.59 * mm});
            skCircle(sketch, "E201.MirrorC", {"center": v(187.33, 73.03) * mm, "radius": 1.59 * mm});
            skCircle(sketch, "E202.MirrorC", {"center": v(142.87, 85.72) * mm, "radius": 1.59 * mm});
            skCircle(sketch, "E203.MirrorC", {"center": v(241.3, 92.07) * mm, "radius": 1.59 * mm});
            skCircle(sketch, "E204.MirrorC", {"center": v(123.83, 85.72) * mm, "radius": 1.59 * mm});
            skCircle(sketch, "E205.MirrorC", {"center": v(269.87, 79.37) * mm, "radius": 1.59 * mm});
            skCircle(sketch, "E206.MirrorC", {"center": v(152.4, 92.08) * mm, "radius": 1.59 * mm});
            skCircle(sketch, "E207.MirrorC", {"center": v(298.45, 85.72) * mm, "radius": 1.59 * mm});
            skCircle(sketch, "E208.MirrorC", {"center": v(200.03, 73.02) * mm, "radius": 1.59 * mm});
            skCircle(sketch, "E209.MirrorC", {"center": v(241.3, 79.37) * mm, "radius": 1.59 * mm});
            skCircle(sketch, "E210.MirrorC", {"center": v(257.17, 79.37) * mm, "radius": 1.59 * mm});
            skCircle(sketch, "E211.MirrorC", {"center": v(311.15, 92.07) * mm, "radius": 1.59 * mm});
            skCircle(sketch, "E212.MirrorC", {"center": v(257.18, 85.72) * mm, "radius": 1.59 * mm});
            skCircle(sketch, "E213.MirrorC", {"center": v(263.53, 92.07) * mm, "radius": 1.59 * mm});
            skCircle(sketch, "E214.MirrorC", {"center": v(117.48, 73.03) * mm, "radius": 1.59 * mm});
            skCircle(sketch, "E215.MirrorC", {"center": v(228.6, 79.37) * mm, "radius": 1.59 * mm});
            skCircle(sketch, "E216.MirrorC", {"center": v(276.23, 92.07) * mm, "radius": 1.59 * mm});
            skCircle(sketch, "E217.MirrorC", {"center": v(95.25, 92.08) * mm, "radius": 1.59 * mm});
            skCircle(sketch, "E218.MirrorC", {"center": v(282.58, 92.07) * mm, "radius": 1.59 * mm});
            skCircle(sketch, "E219.MirrorC", {"center": v(95.25, 73.03) * mm, "radius": 1.59 * mm});
            skCircle(sketch, "E220.MirrorC", {"center": v(222.25, 85.72) * mm, "radius": 1.59 * mm});
            skCircle(sketch, "E221.MirrorC", {"center": v(130.18, 92.08) * mm, "radius": 1.59 * mm});
            skCircle(sketch, "E222.MirrorC", {"center": v(212.72, 73.02) * mm, "radius": 1.59 * mm});
            skCircle(sketch, "E223.MirrorC", {"center": v(269.87, 85.72) * mm, "radius": 1.59 * mm});
            skCircle(sketch, "E224.MirrorC", {"center": v(101.6, 73.03) * mm, "radius": 1.59 * mm});
            skCircle(sketch, "E225.MirrorC", {"center": v(101.6, 79.37) * mm, "radius": 1.59 * mm});
            skCircle(sketch, "E226.MirrorC", {"center": v(142.88, 73.03) * mm, "radius": 1.59 * mm});
            skCircle(sketch, "E227.MirrorC", {"center": v(165.1, 85.72) * mm, "radius": 1.59 * mm});
            skCircle(sketch, "E228.MirrorC", {"center": v(130.17, 79.37) * mm, "radius": 1.59 * mm});
            skCircle(sketch, "E229.MirrorC", {"center": v(177.8, 85.72) * mm, "radius": 1.59 * mm});
            skCircle(sketch, "E230.MirrorC", {"center": v(82.55, 85.72) * mm, "radius": 1.59 * mm});
            skCircle(sketch, "E231.MirrorC", {"center": v(158.75, 73.03) * mm, "radius": 1.59 * mm});
            skCircle(sketch, "E232.MirrorC", {"center": v(298.45, 73.02) * mm, "radius": 1.59 * mm});
            skCircle(sketch, "E233.MirrorC", {"center": v(241.3, 85.72) * mm, "radius": 1.59 * mm});
            skCircle(sketch, "E234.MirrorC", {"center": v(206.38, 92.07) * mm, "radius": 1.59 * mm});
            skCircle(sketch, "E235.MirrorC", {"center": v(177.8, 73.03) * mm, "radius": 1.59 * mm});
            skCircle(sketch, "E236.MirrorC", {"center": v(136.52, 79.37) * mm, "radius": 1.59 * mm});
            skCircle(sketch, "E237.MirrorC", {"center": v(123.82, 79.37) * mm, "radius": 1.59 * mm});
            skCircle(sketch, "E238.MirrorC", {"center": v(298.45, 79.37) * mm, "radius": 1.59 * mm});
            skCircle(sketch, "E239.MirrorC", {"center": v(193.68, 92.07) * mm, "radius": 1.59 * mm});
            skCircle(sketch, "E240.MirrorC", {"center": v(107.95, 73.03) * mm, "radius": 1.59 * mm});
            skCircle(sketch, "E241.MirrorC", {"center": v(241.3, 73.02) * mm, "radius": 1.59 * mm});
            skCircle(sketch, "E242.MirrorC", {"center": v(292.1, 79.37) * mm, "radius": 1.59 * mm});
            skCircle(sketch, "E243.MirrorC", {"center": v(95.25, 79.37) * mm, "radius": 1.59 * mm});
            skCircle(sketch, "E244.MirrorC", {"center": v(317.5, 92.07) * mm, "radius": 1.59 * mm});
            skCircle(sketch, "E245.MirrorC", {"center": v(193.68, 73.02) * mm, "radius": 1.59 * mm});
            skCircle(sketch, "E246.MirrorC", {"center": v(234.95, 85.72) * mm, "radius": 1.59 * mm});
            skCircle(sketch, "E247.MirrorC", {"center": v(107.95, 85.72) * mm, "radius": 1.59 * mm});
            skCircle(sketch, "E248.MirrorC", {"center": v(101.6, 92.08) * mm, "radius": 1.59 * mm});
            skCircle(sketch, "E249.MirrorC", {"center": v(200.03, 92.07) * mm, "radius": 1.59 * mm});
            skCircle(sketch, "E250.MirrorC", {"center": v(200.02, 79.37) * mm, "radius": 1.59 * mm});
            skCircle(sketch, "E251.MirrorC", {"center": v(152.4, 85.72) * mm, "radius": 1.59 * mm});
            skCircle(sketch, "E252.MirrorC", {"center": v(107.95, 79.37) * mm, "radius": 1.59 * mm});
            skCircle(sketch, "E253.MirrorC", {"center": v(158.75, 79.37) * mm, "radius": 1.59 * mm});
            skCircle(sketch, "E254.MirrorC", {"center": v(228.6, 92.07) * mm, "radius": 1.59 * mm});
            skCircle(sketch, "E255.MirrorC", {"center": v(257.18, 92.07) * mm, "radius": 1.59 * mm});
            skCircle(sketch, "E256.MirrorC", {"center": v(193.68, 85.72) * mm, "radius": 1.59 * mm});
            skCircle(sketch, "E257.MirrorC", {"center": v(212.72, 79.37) * mm, "radius": 1.59 * mm});
            skCircle(sketch, "E258.MirrorC", {"center": v(142.88, 92.08) * mm, "radius": 1.59 * mm});
            skCircle(sketch, "E259.MirrorC", {"center": v(117.47, 79.37) * mm, "radius": 1.59 * mm});
            skCircle(sketch, "E260.MirrorC", {"center": v(247.65, 73.02) * mm, "radius": 1.59 * mm});
            skCircle(sketch, "E261.MirrorC", {"center": v(263.52, 79.37) * mm, "radius": 1.59 * mm});
            skCircle(sketch, "E262.MirrorC", {"center": v(88.9, 73.03) * mm, "radius": 1.59 * mm});
            skCircle(sketch, "E263.MirrorC", {"center": v(222.25, 73.02) * mm, "radius": 1.59 * mm});
            skCircle(sketch, "E264.MirrorC", {"center": v(263.53, 85.72) * mm, "radius": 1.59 * mm});
            skCircle(sketch, "E265.MirrorC", {"center": v(101.6, 85.72) * mm, "radius": 1.59 * mm});
            skCircle(sketch, "E266.MirrorC", {"center": v(187.32, 79.37) * mm, "radius": 1.59 * mm});
            skCircle(sketch, "E267.MirrorC", {"center": v(298.45, 92.07) * mm, "radius": 1.59 * mm});
            skCircle(sketch, "E268.MirrorC", {"center": v(200.02, 85.72) * mm, "radius": 1.59 * mm});
            skCircle(sketch, "E269.MirrorC", {"center": v(212.73, 92.07) * mm, "radius": 1.59 * mm});
            skCircle(sketch, "E270.MirrorC", {"center": v(311.15, 79.37) * mm, "radius": 1.59 * mm});
            skCircle(sketch, "E271.MirrorC", {"center": v(311.15, 85.72) * mm, "radius": 1.59 * mm});
            skCircle(sketch, "E272.MirrorC", {"center": v(282.57, 79.37) * mm, "radius": 1.59 * mm});
            skCircle(sketch, "E273.MirrorC", {"center": v(152.4, 79.37) * mm, "radius": 1.59 * mm});
            skCircle(sketch, "E274.MirrorC", {"center": v(171.45, 85.72) * mm, "radius": 1.59 * mm});
            skCircle(sketch, "E275.MirrorC", {"center": v(165.1, 79.37) * mm, "radius": 1.59 * mm});
            skCircle(sketch, "E276.MirrorC", {"center": v(311.15, 73.02) * mm, "radius": 1.59 * mm});
            skCircle(sketch, "E277.MirrorC", {"center": v(292.1, 85.72) * mm, "radius": 1.59 * mm});
            skCircle(sketch, "E278.MirrorC", {"center": v(171.45, 73.03) * mm, "radius": 1.59 * mm});
            skCircle(sketch, "E279.MirrorC", {"center": v(177.8, 92.07) * mm, "radius": 1.59 * mm});
            skCircle(sketch, "E280.MirrorC", {"center": v(88.9, 85.72) * mm, "radius": 1.59 * mm});
            skCircle(sketch, "E281.MirrorC", {"center": v(206.37, 79.37) * mm, "radius": 1.59 * mm});
            skCircle(sketch, "E282.MirrorC", {"center": v(269.87, 73.02) * mm, "radius": 1.59 * mm});
            skCircle(sketch, "E283.MirrorC", {"center": v(158.75, 92.08) * mm, "radius": 1.59 * mm});
            skCircle(sketch, "E284.MirrorC", {"center": v(228.6, 73.02) * mm, "radius": 1.59 * mm});
            skCircle(sketch, "E285.MirrorC", {"center": v(107.95, 92.08) * mm, "radius": 1.59 * mm});
            skCircle(sketch, "E286.MirrorC", {"center": v(282.57, 85.72) * mm, "radius": 1.59 * mm});
            skCircle(sketch, "E287.MirrorC", {"center": v(228.6, 85.72) * mm, "radius": 1.59 * mm});
            skCircle(sketch, "E288.MirrorC", {"center": v(136.53, 92.08) * mm, "radius": 1.59 * mm});
            skCircle(sketch, "E289.MirrorC", {"center": v(82.97, 73.03) * mm, "radius": 1.59 * mm});
            skCircle(sketch, "E290.MirrorC", {"center": v(234.95, 79.37) * mm, "radius": 1.59 * mm});
            skCircle(sketch, "E291.MirrorC", {"center": v(292.1, 92.07) * mm, "radius": 1.59 * mm});
            skCircle(sketch, "E292.MirrorC", {"center": v(276.22, 73.02) * mm, "radius": 1.59 * mm});
            skCircle(sketch, "E293.MirrorC", {"center": v(269.88, 92.07) * mm, "radius": 1.59 * mm});
            skCircle(sketch, "E294.MirrorC", {"center": v(317.5, 85.72) * mm, "radius": 1.59 * mm});
            skCircle(sketch, "E295.MirrorC", {"center": v(206.37, 85.72) * mm, "radius": 1.59 * mm});
            skCircle(sketch, "E296.MirrorC", {"center": v(88.9, 79.37) * mm, "radius": 1.59 * mm});
            skCircle(sketch, "E297.MirrorC", {"center": v(276.22, 79.37) * mm, "radius": 1.59 * mm});
            skCircle(sketch, "E298.MirrorC", {"center": v(130.17, 85.72) * mm, "radius": 1.59 * mm});
            skCircle(sketch, "E299.MirrorC", {"center": v(130.18, 73.03) * mm, "radius": 1.59 * mm});
            skCircle(sketch, "E300.MirrorC", {"center": v(123.83, 73.03) * mm, "radius": 1.59 * mm});
            skCircle(sketch, "E301.MirrorC", {"center": v(247.65, 85.72) * mm, "radius": 1.59 * mm});
            skCircle(sketch, "E302.MirrorC", {"center": v(177.8, 79.37) * mm, "radius": 1.59 * mm});
            skCircle(sketch, "E303.MirrorC", {"center": v(304.8, 79.37) * mm, "radius": 1.59 * mm});
            skCircle(sketch, "E304.MirrorC", {"center": v(165.1, 92.08) * mm, "radius": 1.59 * mm});
            skCircle(sketch, "E305.MirrorC", {"center": v(247.65, 79.37) * mm, "radius": 1.59 * mm});
            skCircle(sketch, "E306.MirrorC", {"center": v(171.45, 79.37) * mm, "radius": 1.59 * mm});
            skCircle(sketch, "E307.MirrorC", {"center": v(187.33, 92.07) * mm, "radius": 1.59 * mm});
            skCircle(sketch, "E308.MirrorC", {"center": v(152.4, 73.03) * mm, "radius": 1.59 * mm});
            skCircle(sketch, "E309.MirrorC", {"center": v(165.1, 73.03) * mm, "radius": 1.59 * mm});
            skCircle(sketch, "E310.MirrorC", {"center": v(234.95, 73.02) * mm, "radius": 1.59 * mm});
            skCircle(sketch, "E311.MirrorC", {"center": v(304.8, 85.72) * mm, "radius": 1.59 * mm});
            skCircle(sketch, "E312.MirrorC", {"center": v(276.22, 85.72) * mm, "radius": 1.59 * mm});
            skCircle(sketch, "E313.MirrorC", {"center": v(136.52, 85.72) * mm, "radius": 1.59 * mm});
            skCircle(sketch, "E314.1.0.0", {"center": v(73.45, 38.1) * mm, "radius": 1.59 * mm});
            skCircle(sketch, "E314.1.0.1", {"center": v(73.02, 31.75) * mm, "radius": 1.59 * mm});
            skCircle(sketch, "E314.1.0.2", {"center": v(73.03, 25.4) * mm, "radius": 1.59 * mm});
            skCircle(sketch, "E314.1.0.3", {"center": v(73.03, 19.05) * mm, "radius": 1.59 * mm});
            skLineSegment(sketch, "E314.direction1", {"start": v(82.97, 38.1) * mm, "end": v(73.45, 38.1) * mm, "construction": true});
            skLineSegment(sketch, "E315", {"start": v(82.97, 38.1) * mm, "end": v(82.97, 73.03) * mm});
            skLineSegment(sketch, "E316", {"start": v(82.97, 55.56) * mm, "end": v(73.45, 55.56) * mm});
            skLineSegment(sketch, "E317", {"start": v(73.45, 55.56) * mm, "end": v(73.45, 38.1) * mm});
            skCircle(sketch, "E318.1.0", {"center": v(61.1, 43.21) * mm, "radius": 1.59 * mm});
            skCircle(sketch, "E318.1.1", {"center": v(56.31, 39.02) * mm, "radius": 1.59 * mm});
            skCircle(sketch, "E318.1.2", {"center": v(51.82, 34.53) * mm, "radius": 1.59 * mm});
            skCircle(sketch, "E318.1.3", {"center": v(47.33, 30.04) * mm, "radius": 1.59 * mm});
            skCircle(sketch, "E318.2.0", {"center": v(55.98, 55.56) * mm, "radius": 1.59 * mm});
            skCircle(sketch, "E318.2.1", {"center": v(49.64, 55.99) * mm, "radius": 1.59 * mm});
            skCircle(sketch, "E318.2.2", {"center": v(43.29, 55.99) * mm, "radius": 1.59 * mm});
            skCircle(sketch, "E318.2.3", {"center": v(36.94, 55.99) * mm, "radius": 1.59 * mm});
            skCircle(sketch, "E318.3.0", {"center": v(61.1, 67.91) * mm, "radius": 1.59 * mm});
            skCircle(sketch, "E318.3.1", {"center": v(56.91, 72.7) * mm, "radius": 1.59 * mm});
            skCircle(sketch, "E318.3.2", {"center": v(52.42, 77.2) * mm, "radius": 1.59 * mm});
            skCircle(sketch, "E318.3.3", {"center": v(47.93, 81.68) * mm, "radius": 1.59 * mm});
            skCircle(sketch, "E318.4.0", {"center": v(73.45, 73.03) * mm, "radius": 1.59 * mm});
            skCircle(sketch, "E318.4.1", {"center": v(73.87, 79.37) * mm, "radius": 1.59 * mm});
            skCircle(sketch, "E318.4.2", {"center": v(73.87, 85.72) * mm, "radius": 1.59 * mm});
            skCircle(sketch, "E318.4.3", {"center": v(73.87, 92.08) * mm, "radius": 1.59 * mm});
            skPoint(sketch, "E318.center", {"position": v(73.45, 55.56) * mm});
            skLineSegment(sketch, "E318.anchor1", {"start": v(73.45, 55.56) * mm, "end": v(73.45, 38.1) * mm, "construction": true});
            skLineSegment(sketch, "E318.anchor2", {"start": v(73.45, 55.56) * mm, "end": v(73.45, 73.03) * mm, "construction": true});
            skLineSegment(sketch, "E319", {"start": v(327.16, 82.55) * mm, "end": v(346.2, 82.55) * mm});
            skCircle(sketch, "E320", {"center": v(346.2, 82.55) * mm, "radius": 1.59 * mm});
            skSolve(sketch);
        }
        {
            var Q0;
            Q0 = qSketchRegion(id + "F3", true);
            extrude(context, id + "F4", {"entities" : qUnion([Q0]), "operationType" : NewBodyOperationType.REMOVE, "oppositeDirection" : true, "depth" : 6.35 * mm});
        }
    });
